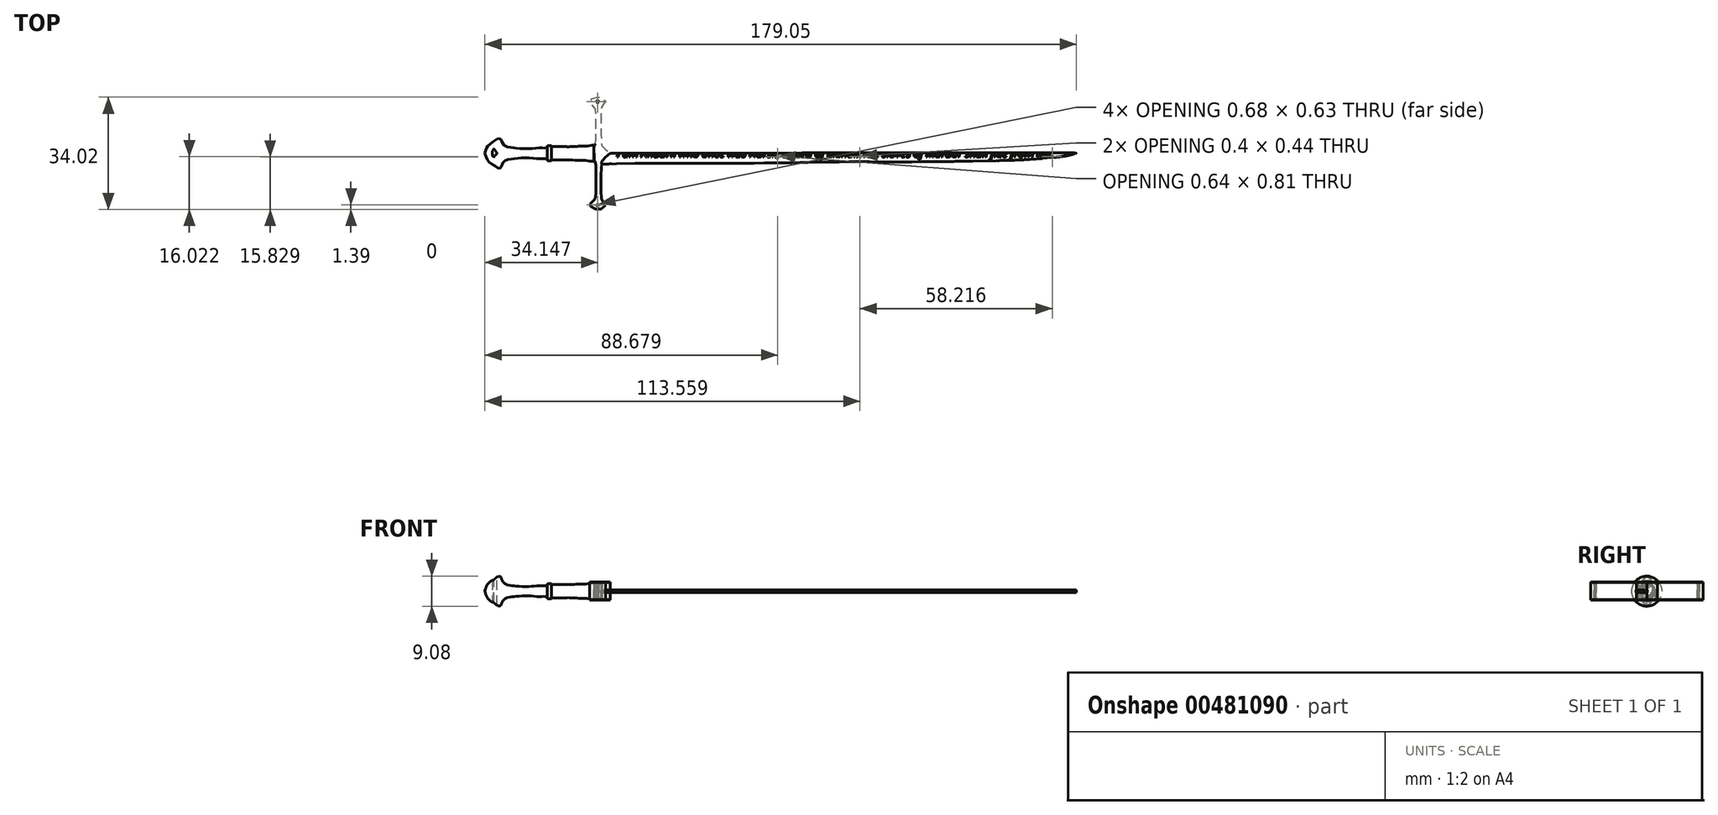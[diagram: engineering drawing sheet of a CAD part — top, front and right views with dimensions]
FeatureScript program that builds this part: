
annotation { "Feature Type Name" : "Feature", "Feature Type Description" : "" }
export const myFeature = defineFeature(function(context is Context, id is Id, definition is map)
    precondition{}
    {
        {
            var Q0;
            Q0=qCreatedBy(makeId("Top.planeOp"),FACE);
            var sketch = newSketch(context, id + "F0", { "sketchPlane" : qUnion([Q0])});
            skLineSegment(sketch, "E0", {"start": v(0, 0) * mm, "end": v(-38.65, 0) * mm});
            skLineSegment(sketch, "E1", {"start": v(-4.07, 0) * mm, "end": v(-4.07, -2.57) * mm});
            skFitSpline(sketch, "E2", {"points": [v(-4.07, -2.57) * mm, v(-5.7, -2.28) * mm, v(-7.34, -2.13) * mm, v(-9.32, -2.1) * mm, v(-11.42, -1.99) * mm, v(-13.02, -2.02) * mm, v(-15.06, -2.07) * mm, v(-16.96, -2.02) * mm], "startDerivative": vector(-12.09, 2.36) * mm, "endDerivative": vector(-12.8, 0.6) * mm});
            skLineSegment(sketch, "E3", {"start": v(-16.96, -2.02) * mm, "end": v(-16.96, -2.25) * mm});
            skLineSegment(sketch, "E4", {"start": v(-16.96, -2.25) * mm, "end": v(-18.25, -2.25) * mm});
            skLineSegment(sketch, "E5", {"start": v(-18.25, -2.25) * mm, "end": v(-18.25, -2.02) * mm});
            skFitSpline(sketch, "E6", {"points": [v(-18.25, -2.02) * mm, v(-18.57, -1.65) * mm, v(-20.55, -1.65) * mm, v(-23.91, -1.38) * mm, v(-27.12, -1.53) * mm, v(-29.5, -1.77) * mm, v(-31.58, -2.7) * mm, v(-32.52, -4.5) * mm, v(-34.23, -3.73) * mm, v(-36.18, -2.25) * mm, v(-37.12, 0) * mm], "startDerivative": vector(-4.51, 9.24) * mm, "endDerivative": vector(-6.65, 23.24) * mm});
            skSolve(sketch);
        }
        {
            var Q0;
            {var subQ0=sQuery(id+"F0.wireOp",EDGE,"E1");Q0=makeQuery(id+"F0.imprint","IMPRINT",FACE,{"disambiguationData":[TD([[makeQuery(id+"F0.imprint","IMPRINT",EDGE,{"derivedFrom":subQ0}),-1.0]])]});}
            var Q1;
            Q1=sQuery(id+"F0.wireOp",EDGE,"E0");
            revolve(context, id + "F1", {"entities" : qUnion([Q0]), "axis" : qUnion([Q1]), "revolveType" : RevolveType.FULL});
        }
        {
            var Q0;
            Q0=qCreatedBy(makeId("Top.planeOp"),FACE);
            var sketch = newSketch(context, id + "F2", { "sketchPlane" : qUnion([Q0])});
            skLineSegment(sketch, "E7", {"start": v(-34.33, 1.35) * mm, "end": v(-33.38, 0) * mm});
            skLineSegment(sketch, "E8", {"start": v(-33.38, 0) * mm, "end": v(-34.48, -1.25) * mm});
            skFitSpline(sketch, "E9", {"points": [v(-34.48, -1.25) * mm, v(-34.75, -0.72) * mm, v(-34.87, 0) * mm, v(-34.7, 0.76) * mm, v(-34.33, 1.35) * mm], "startDerivative": vector(-1.28, 2.17) * mm, "endDerivative": vector(1.6, 2.24) * mm});
            skSolve(sketch);
        }
        {
            var Q0;
            Q0 = qSketchRegion(id + "F2", true);
            extrude(context, id + "F3", {"entities" : qUnion([Q0]), "operationType" : NewBodyOperationType.ADD, "oppositeDirection" : true, "depth" : 2.3 * mm});
        }
        {
            var Q0;
            Q0=qCreatedBy(makeId("Top.planeOp"),FACE);
            var sketch = newSketch(context, id + "F4", { "sketchPlane" : qUnion([Q0])});
            skLineSegment(sketch, "E10", {"start": v(-34.35, 1.36) * mm, "end": v(-33.42, 0) * mm});
            skLineSegment(sketch, "E11", {"start": v(-33.42, 0) * mm, "end": v(-34.47, -1.24) * mm});
            skFitSpline(sketch, "E12", {"points": [v(-34.47, -1.24) * mm, v(-34.79, -0.7) * mm, v(-34.9, 0) * mm, v(-34.78, 0.76) * mm, v(-34.35, 1.36) * mm], "startDerivative": vector(-1.55, 2.18) * mm, "endDerivative": vector(1.96, 2.2) * mm});
            skSolve(sketch);
        }
        {
            var Q0;
            Q0 = qSketchRegion(id + "F4", true);
            extrude(context, id + "F5", {"entities" : qUnion([Q0]), "operationType" : NewBodyOperationType.REMOVE, "endBound" : BoundingType.THROUGH_ALL, "oppositeDirection" : true, "depth" : 25.4 * mm, "hasSecondDirection" : true, "secondDirectionBound" : SecondDirectionBoundingType.THROUGH_ALL, "secondDirectionOppositeDirection" : false, "secondDirectionDepth" : 25.4 * mm});
        }
        {
            var Q0;
            Q0=qCreatedBy(makeId("Top.planeOp"),FACE);
            var sketch = newSketch(context, id + "F6", { "sketchPlane" : qUnion([Q0])});
            skLineSegment(sketch, "E13", {"start": v(0, 0) * mm, "end": v(-8.4, 0) * mm});
            skFitSpline(sketch, "E14", {"points": [v(-4.02, 0) * mm, v(-4.07, -2.49) * mm, v(-4.06, -2.5) * mm, v(-3.82, -2.5) * mm, v(-3.8, -2.53) * mm, v(-3.74, -2.76) * mm, v(-3.54, -3.6) * mm, v(-3.43, -5.52) * mm, v(-3.47, -9.21) * mm, v(-3.54, -12.12) * mm, v(-3.76, -13.79) * mm, v(-5.33, -15.52) * mm, v(-5.29, -15.68) * mm, v(-4.9, -16.28) * mm, v(-3.12, -16.98) * mm, v(-1.58, -16.7) * mm, v(-0.59, -15.68) * mm, v(-0.59, -15.54) * mm, v(-1.37, -14.88) * mm, v(-2, -12.36) * mm, v(-1.97, -9.15) * mm, v(-1.96, -5.8) * mm, v(-1.62, -3.24) * mm, v(-1.63, -3.22) * mm, v(-1.83, -3.22) * mm, v(-1.85, -3.18) * mm, v(-1.85, -2.82) * mm, v(-1.1, -1.65) * mm, v(0.84, 0) * mm], "startDerivative": vector(-0.85, -65.73) * mm, "endDerivative": vector(38.65, 29.63) * mm});
            skLineSegment(sketch, "E15", {"start": v(0, 0) * mm, "end": v(1.34, 0) * mm});
            skSolve(sketch);
        }
        {
            var Q0;
            Q0 = qSketchRegion(id + "F6", true);
            extrude(context, id + "F7", {"entities" : qUnion([Q0]), "depth" : 2.62 * mm, "hasSecondDirection" : true, "secondDirectionOppositeDirection" : true, "secondDirectionDepth" : 2.74 * mm});
        }
        {
            var Q0;
            Q0=qCreatedBy(makeId("Top.planeOp"),FACE);
            var sketch = newSketch(context, id + "F8", { "sketchPlane" : qUnion([Q0])});
            skLineSegment(sketch, "E16", {"start": v(-3, -15.3) * mm, "end": v(-2.63, -15.78) * mm});
            skLineSegment(sketch, "E17", {"start": v(-3, -15.3) * mm, "end": v(-3.31, -15.78) * mm});
            skFitSpline(sketch, "E18", {"points": [v(-3.31, -15.78) * mm, v(-3.27, -15.86) * mm, v(-3.2, -15.9) * mm, v(-3.08, -15.93) * mm, v(-2.88, -15.91) * mm, v(-2.74, -15.86) * mm, v(-2.63, -15.78) * mm], "startDerivative": vector(0.27, -0.6) * mm, "endDerivative": vector(0.61, 0.44) * mm});
            skSolve(sketch);
        }
        {
            var Q0;
            Q0 = qSketchRegion(id + "F8", true);
            extrude(context, id + "F9", {"entities" : qUnion([Q0]), "operationType" : NewBodyOperationType.REMOVE, "endBound" : BoundingType.THROUGH_ALL, "depth" : 25.4 * mm});
        }
        {
            var Q0;
            Q0 = qSketchRegion(id + "F8", true);
            extrude(context, id + "F10", {"entities" : qUnion([Q0]), "operationType" : NewBodyOperationType.REMOVE, "endBound" : BoundingType.THROUGH_ALL, "oppositeDirection" : true, "depth" : 25.4 * mm});
        }
        {
            var Q0;
            Q0 = qSketchRegion(id + "F8", true);
            extrude(context, id + "F11", {"entities" : qUnion([Q0]), "operationType" : NewBodyOperationType.REMOVE, "endBound" : BoundingType.THROUGH_ALL, "depth" : 25.4 * mm});
        }
        {
            var Q0;
            Q0=makeQuery(id+"F7.opExtrude","SWEPT_BODY",BODY,{"disambiguationData":[OSD([sQuery(id+"F6.wireOp",EDGE,"E13"),sQuery(id+"F6.wireOp",EDGE,"E14"),sQuery(id+"F6.wireOp",EDGE,"E15")])]});
            var Q1;
            Q1=qCreatedBy(makeId("Front.planeOp"),FACE);
            mirror(context, id + "F12", {"operationType" : NewBodyOperationType.ADD, "entities" : qUnion([Q0]), "mirrorPlane" : qUnion([Q1])});
        }
        {
            var Q0;
            Q0=qCreatedBy(makeId("Top.planeOp"),FACE);
            var sketch = newSketch(context, id + "F13", { "sketchPlane" : qUnion([Q0])});
            skLineSegment(sketch, "E19", {"start": v(0.8, 0) * mm, "end": v(142.49, 0.2) * mm});
            skFitSpline(sketch, "E20", {"points": [v(0.8, 0) * mm, v(0, -0.54) * mm, v(-1.26, -1.62) * mm, v(-2, -2.76) * mm, v(-2.03, -3.18) * mm, v(-2.03, -3.21) * mm, v(1.34, -3.2) * mm, v(11.3, -3) * mm, v(20.26, -3.05) * mm, v(35.78, -3.05) * mm, v(55.61, -2.84) * mm, v(68.52, -2.6) * mm, v(90.78, -2.6) * mm, v(106.57, -2.43) * mm, v(117.55, -2.23) * mm, v(125.49, -1.98) * mm, v(133.78, -1.38) * mm, v(142.49, 0.2) * mm], "startDerivative": vector(-34.44, -21.98) * mm, "endDerivative": vector(123.92, 47.67) * mm});
            skSolve(sketch);
        }
        {
            var Q0;
            Q0 = qSketchRegion(id + "F13", true);
            extrude(context, id + "F14", {"entities" : qUnion([Q0]), "operationType" : NewBodyOperationType.ADD, "depth" : 0.4 * mm});
        }
        {
            var Q0;
            {var subQ0=sQuery(id+"F13.wireOp",EDGE,"E19");var subQ1=sQuery(id+"F13.wireOp",EDGE,"3c1c5b50-c5d9-44e4-a03a-cb502a0039ae");Q0=makeQuery(id+"Fvn0MWFNnOrBU2Z_2.1.F14.boolean.opBoolean","MERGE",FACE,{"derivedFrom":[makeQuery(id+"F14.opExtrude","CAP_FACE",FACE,{"disambiguationData":[OSD([subQ1,subQ0])],"isStart":false}),makeQuery(id+"Fvn0MWFNnOrBU2Z_2.1.F14.opExtrude","CAP_FACE",FACE,{"disambiguationData":[OSD([subQ1,subQ0])],"isStart":false})]});}
            var sketch = newSketch(context, id + "F15", { "sketchPlane" : qUnion([Q0])});
            skText(sketch, "E21", { "text": " I am Andúril who once was Narsil, sword of Elendil.The slaves of Mordor shall flee from me.", "fontName": "OpenSans-Italic.ttf"});
            const initialGuessF15  = {"E21": [0.00193, -0.00116, 1, 0, 0.00238]};
            skSetInitialGuess(sketch, initialGuessF15);
            skSolve(sketch);
        }
        {
            var Q0;
            Q0 = qSketchRegion(id + "F15", true);
            extrude(context, id + "F16", {"entities" : qUnion([Q0]), "operationType" : NewBodyOperationType.REMOVE, "oppositeDirection" : true, "depth" : 0.03 * mm});
        }
        {
            var Q0;
            {var subQ0=sQuery(id+"F13.wireOp",EDGE,"E19");var subQ1=sQuery(id+"F13.wireOp",EDGE,"3c1c5b50-c5d9-44e4-a03a-cb502a0039ae");Q0=makeQuery(id+"Fvn0MWFNnOrBU2Z_2.1.F14.boolean.opBoolean","MERGE",FACE,{"derivedFrom":[makeQuery(id+"F14.opExtrude","CAP_FACE",FACE,{"disambiguationData":[OSD([subQ1,subQ0])],"isStart":true}),makeQuery(id+"Fvn0MWFNnOrBU2Z_2.1.F14.opExtrude","CAP_FACE",FACE,{"disambiguationData":[OSD([subQ1,subQ0])],"isStart":true})]});}
            var sketch = newSketch(context, id + "F17", { "sketchPlane" : qUnion([Q0])});
            skSolve(sketch);
        }
        {
            var Q0;
            Q0=makeQuery(id+"F7.opExtrude","SWEPT_BODY",BODY,{"disambiguationData":[OSD([sQuery(id+"F6.wireOp",EDGE,"E13"),sQuery(id+"F6.wireOp",EDGE,"E14"),sQuery(id+"F6.wireOp",EDGE,"E15")])]});
            var Q1;
            Q1=qCreatedBy(makeId("Top.planeOp"),FACE);
            mirror(context, id + "F18", {"operationType" : NewBodyOperationType.ADD, "entities" : qUnion([Q0]), "mirrorPlane" : qUnion([Q1])});
        }
        {
            var Q0;
            {var subQ0=sQuery(id+"F13.wireOp",EDGE,"E20");var subQ1=sQuery(id+"F13.wireOp",EDGE,"E19");var subQ2=makeQuery(id+"F7.opExtrude","SWEPT_FACE",FACE,{"disambiguationData":[OSD([sQuery(id+"F6.wireOp",EDGE,"E14")])]});Q0=makeQuery(id+"F16.boolean.opBoolean","SPLIT",FACE,{"disambiguationData":[TD([subQ2])],"derivedFrom":makeQuery(id+"Fvn0MWFNnOrBU2Z_2.1.F14.boolean.opBoolean","MERGE",FACE,{"derivedFrom":[makeQuery(id+"F14.opExtrude","CAP_FACE",FACE,{"disambiguationData":[OSD([subQ1,subQ0])],"isStart":false}),makeQuery(id+"Fvn0MWFNnOrBU2Z_2.1.F14.opExtrude","CAP_FACE",FACE,{"disambiguationData":[OSD([subQ1,subQ0])],"isStart":false})]})});}
            var sketch = newSketch(context, id + "F19", { "sketchPlane" : qUnion([Q0])});
            skLineSegment(sketch, "E22", {"start": v(141.3, 0.2) * mm, "end": v(141.93, 0) * mm});
            skLineSegment(sketch, "E23", {"start": v(141.93, 0) * mm, "end": v(141.3, -0.2) * mm});
            skLineSegment(sketch, "E24", {"start": v(141.93, 0) * mm, "end": v(142.49, 0.2) * mm});
            skLineSegment(sketch, "E25", {"start": v(142.49, 0.2) * mm, "end": v(141.3, 0.2) * mm});
            skLineSegment(sketch, "E26", {"start": v(141.93, 0) * mm, "end": v(142.49, -0.2) * mm});
            skLineSegment(sketch, "E27", {"start": v(142.49, -0.2) * mm, "end": v(141.3, -0.2) * mm});
            skSolve(sketch);
        }
        {
            var Q0;
            Q0 = qSketchRegion(id + "F19", true);
            extrude(context, id + "F20", {"entities" : qUnion([Q0]), "operationType" : NewBodyOperationType.REMOVE, "endBound" : BoundingType.THROUGH_ALL, "oppositeDirection" : true, "depth" : 25.4 * mm});
        }
    });
